# Revit family: Буст-I_ЕС_Eng
name_source: partatom
category: Mechanical Equipment
units: mm (PartAtom-declared; Revit-internal decimal feet)

## family parameters
Always vertical = Yes
Classification = None
Cut with Voids When Loaded = No
Part Type = Normal
Room Calculation Point = No
Round Connector Dimension = Use Diameter
Shared = No
Work Plane-Based = No

## types (8) — shared parameters
00_20_Manufacturer = Vents
00_20_Name = Sound-insulated fan
Amperage = 1 A
Casing Material = Steel, galvanized
Frequency = 50 Hz
L = 739 mm  [stored 2.42454 ft]
L1 = 601 mm  [stored 1.97178 ft]
Length = 739 mm  [stored 2.42454 ft]
Load Classification = HVAC
Maintenance zone material = <By Category>
Manufacturer = Vents
Number of Fase = 1
URL = https://ventilation-system.com
Voltage = 230 V
zero-valued in all types: Default Elevation

## per-type parameters (varying)
| type | Apparent Load | B | D | D1 | Diameter | Dy | Height | Maximum Air Flow | Power | Sound pressure level at 3 m distance | Weight | Width | b | d1 |
| Boost-I 150 | 117 VA | 292 mm  [stored 0.958005 ft] | 150 mm | 242 mm  [stored 0.793963 ft] | 150 mm | 145 mm  [stored 0.475722 ft] | 242 mm  [stored 0.793963 ft] | 1110.0 m³/h | 113 W | 44 dBA | 8.20 kg | 292 mm  [stored 0.958005 ft] | 171 mm  [stored 0.561024 ft] | 110 mm  [stored 0.360892 ft] |
| Boost-I 315 | 193 VA | 449 mm  [stored 1.4731 ft] | 315 mm  [stored 1.03346 ft] | 397 mm  [stored 1.30249 ft] | 315 mm  [stored 1.03346 ft] | 310 mm  [stored 1.01706 ft] | 397 mm  [stored 1.30249 ft] | 1670.0 m³/h | 188 W | 45 dBA | 9.50 kg | 449 mm  [stored 1.4731 ft] | 251 mm | 188 mm |
| Boost-I 200 | 117 VA | 339 mm  [stored 1.1122 ft] | 200 mm  [stored 0.656168 ft] | 281 mm  [stored 0.921916 ft] | 200 mm  [stored 0.656168 ft] | 195 mm  [stored 0.639764 ft] | 281 mm  [stored 0.921916 ft] | 1110.0 m³/h | 113 W | 44 dBA | 8.20 kg | 339 mm  [stored 1.1122 ft] | 199 mm | 130 mm |
| Boost-I 250 | 193 VA | 389 mm  [stored 1.27625 ft] | 250 mm  [stored 0.82021 ft] | 337 mm  [stored 1.10564 ft] | 250 mm  [stored 0.82021 ft] | 245 mm  [stored 0.803806 ft] | 337 mm  [stored 1.10564 ft] | 1670.0 m³/h | 188 W | 45 dBA | 9.50 kg | 389 mm  [stored 1.27625 ft] | 221 mm | 158 mm |
| Boost-I 150 ЕС | 221 VA | 292 mm  [stored 0.958005 ft] | 150 mm | 242 mm  [stored 0.793963 ft] | 150 mm | 145 mm  [stored 0.475722 ft] | 242 mm  [stored 0.793963 ft] | 1210.0 m³/h | 121 W | 47 dBA | 8.20 kg | 292 mm  [stored 0.958005 ft] | 171 mm  [stored 0.561024 ft] | 110 mm  [stored 0.360892 ft] |
| Boost-I 200 ЕС | 221 VA | 339 mm  [stored 1.1122 ft] | 200 mm  [stored 0.656168 ft] | 281 mm  [stored 0.921916 ft] | 200 mm  [stored 0.656168 ft] | 195 mm  [stored 0.639764 ft] | 281 mm  [stored 0.921916 ft] | 1210.0 m³/h | 121 W | 47 dBA | 8.20 kg | 339 mm  [stored 1.1122 ft] | 199 mm | 130 mm |
| Boost-I 250 ЕС | 308 VA | 389 mm  [stored 1.27625 ft] | 250 mm  [stored 0.82021 ft] | 337 mm  [stored 1.10564 ft] | 250 mm  [stored 0.82021 ft] | 245 mm  [stored 0.803806 ft] | 337 mm  [stored 1.10564 ft] | 1750.0 m³/h | 168 W | 48 dBA | 9.50 kg | 389 mm  [stored 1.27625 ft] | 221 mm | 158 mm |
| Boost-I 315 ЕС | 308 VA | 449 mm  [stored 1.4731 ft] | 315 mm  [stored 1.03346 ft] | 397 mm  [stored 1.30249 ft] | 315 mm  [stored 1.03346 ft] | 310 mm  [stored 1.01706 ft] | 397 mm  [stored 1.30249 ft] | 1750.0 m³/h | 168 W | 45 dBA | 9.50 kg | 449 mm  [stored 1.4731 ft] | 251 mm | 188 mm |

note: column(s) folded — value = type name in every type: 00_20_Type

note: [stored X ft] marks values corroborated as IEEE doubles in the binary element streams (Revit-internal decimal feet)
